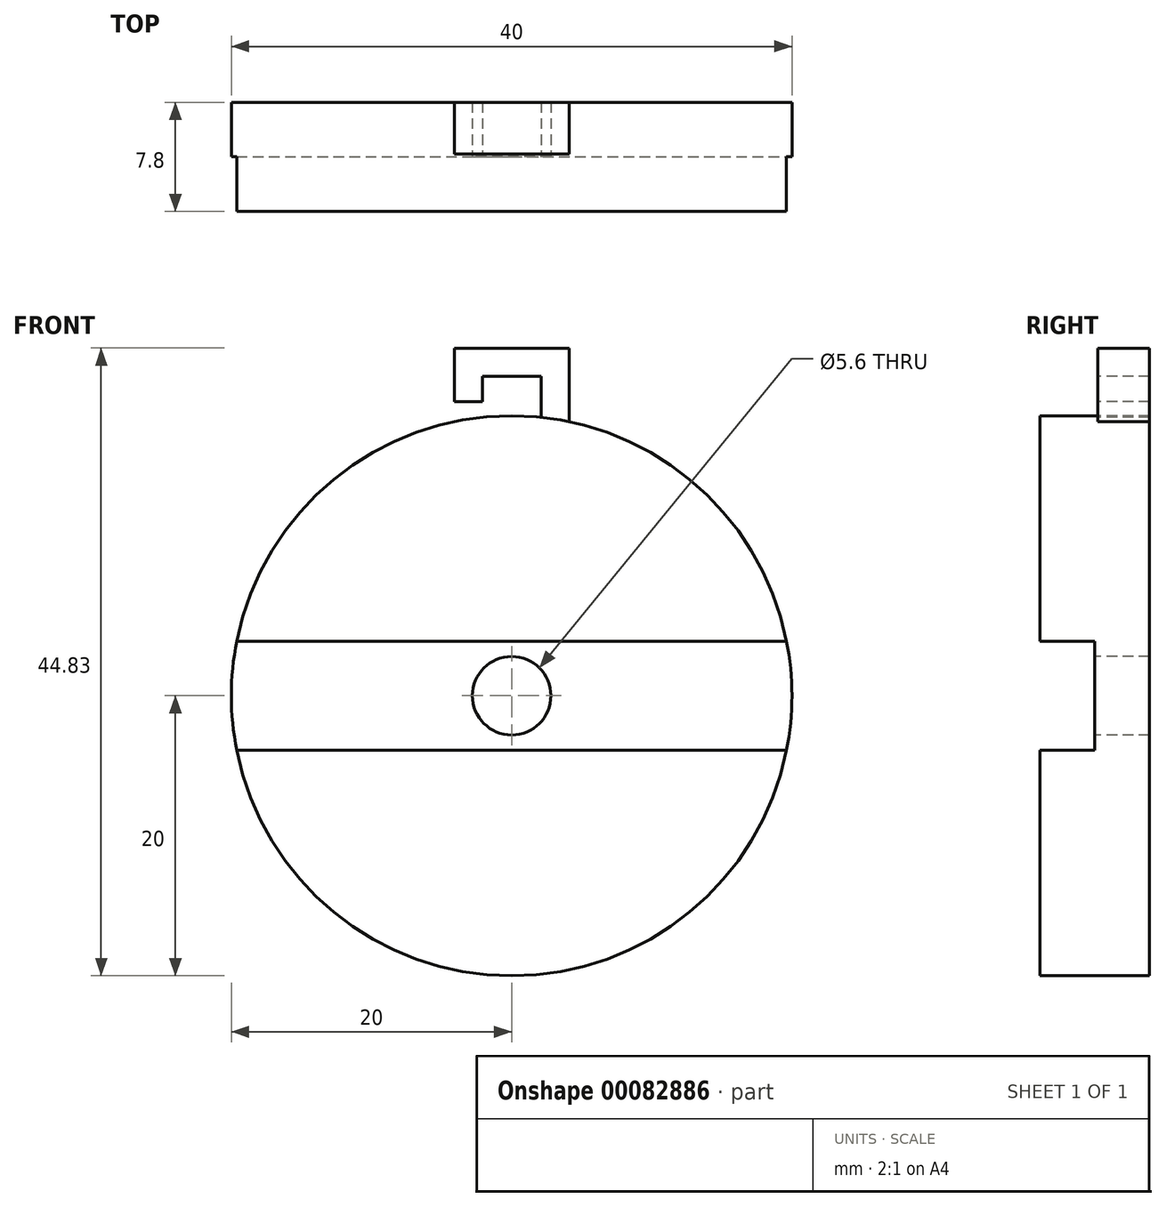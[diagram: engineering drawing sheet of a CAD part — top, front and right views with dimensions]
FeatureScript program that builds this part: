
annotation { "Feature Type Name" : "Feature", "Feature Type Description" : "" }
export const myFeature = defineFeature(function(context is Context, id is Id, definition is map)
    precondition{}
    {
        {
            var Q0;
            Q0=qCreatedBy(makeId("Front.planeOp"),FACE);
            var sketch = newSketch(context, id + "F0", { "sketchPlane" : qUnion([Q0])});
            skCircle(sketch, "E0", {"center": v(0, 0) * mm, "radius": 20 * mm});
            skSolve(sketch);
        }
        {
            var Q0;
            Q0=qSketchRegion(id+"F0",true);
            var Q1;
            Q1=makeQuery(id+"F0.imprint","IMPRINT",FACE,{"disambiguationData":[TD([[makeQuery(id+"F0.imprint","IMPRINT",EDGE,{"derivedFrom":sQuery(id+"F0.wireOp",EDGE,"E0")}),1.0]])]});
            extrude(context, id + "F1", {"entities" : qUnion([Q0, Q1]), "oppositeDirection" : true, "depth" : 7.8 * mm});
        }
        {
            var Q0;
            Q0=makeQuery(id+"F1.opExtrude","CAP_FACE",FACE,{"disambiguationData":[OSD([sQuery(id+"F0.wireOp",EDGE,"E0")])],"isStart":true});
            var sketch = newSketch(context, id + "F2", { "sketchPlane" : qUnion([Q0])});
            skLineSegment(sketch, "E1.bottom", {"start": v(-20, 3.9) * mm, "end": v(20, 3.9) * mm});
            skLineSegment(sketch, "E1.top", {"start": v(-20, -3.9) * mm, "end": v(20, -3.9) * mm});
            skLineSegment(sketch, "E1.left", {"start": v(-20, 3.9) * mm, "end": v(-20, -3.9) * mm});
            skLineSegment(sketch, "E1.right", {"start": v(20, 3.9) * mm, "end": v(20, -3.9) * mm});
            skSolve(sketch);
        }
        {
            var Q0;
            {var subQ0=sQuery(id+"F2.wireOp",EDGE,"E1.bottom");var subQ1=makeQuery(id+"F1.opExtrude","CAP_EDGE",EDGE,{"disambiguationData":[OSD([sQuery(id+"F0.wireOp",EDGE,"E0")])],"isStart":true});var subQ4=makeQuery(id+"F2.imprint","INTERSECT",VERTEX,{"disambiguationData":[OD(0.0)],"derivedFrom":[subQ1,subQ0]});Q0=makeQuery(id+"F2.imprint","IMPRINT",FACE,{"disambiguationData":[TD([[makeQuery(id+"F2.imprint","IMPRINT",EDGE,{"disambiguationData":[TD([[subQ4,-1.0]])],"derivedFrom":subQ0}),-1.0]])]});}
            extrude(context, id + "F3", {"entities" : qUnion([Q0]), "operationType" : NewBodyOperationType.REMOVE, "oppositeDirection" : true, "depth" : 3.9 * mm});
        }
        {
            var Q0;
            Q0=makeQuery(id+"F3.boolean.opBoolean","COPY",FACE,{"derivedFrom":makeQuery(id+"F3.opExtrude","CAP_FACE",FACE,{"disambiguationData":[OSD([sQuery(id+"F0.wireOp",EDGE,"E0"),sQuery(id+"F2.wireOp",EDGE,"E1.bottom"),sQuery(id+"F2.wireOp",EDGE,"E1.top")])],"isStart":false})});
            var sketch = newSketch(context, id + "F4", { "sketchPlane" : qUnion([Q0])});
            skCircle(sketch, "E2", {"center": v(0, 0) * mm, "radius": 2.8 * mm});
            skSolve(sketch);
        }
        {
            var Q0;
            Q0=qSketchRegion(id+"F4",true);
            extrude(context, id + "F5", {"entities" : qUnion([Q0]), "operationType" : NewBodyOperationType.REMOVE, "endBound" : BoundingType.THROUGH_ALL, "oppositeDirection" : true, "depth" : 25 * mm});
        }
        {
            var Q0;
            Q0=makeQuery(id+"F1.opExtrude","CAP_FACE",FACE,{"disambiguationData":[OSD([sQuery(id+"F0.wireOp",EDGE,"E0")])],"isStart":false});
            var sketch = newSketch(context, id + "F6", { "sketchPlane" : qUnion([Q0])});
            skLineSegment(sketch, "E3.bottom", {"start": v(-4.1, 24.83) * mm, "end": v(4.1, 24.83) * mm});
            skLineSegment(sketch, "E3.top", {"start": v(-4.1, 19.58) * mm, "end": v(4.1, 19.58) * mm});
            skLineSegment(sketch, "E3.left", {"start": v(-4.1, 24.83) * mm, "end": v(-4.1, 19.58) * mm});
            skLineSegment(sketch, "E3.right", {"start": v(4.1, 24.83) * mm, "end": v(4.1, 19.58) * mm});
            skSolve(sketch);
        }
        {
            var Q0;
            Q0=qSketchRegion(id+"F6",true);
            extrude(context, id + "F7", {"entities" : qUnion([Q0]), "operationType" : NewBodyOperationType.ADD, "oppositeDirection" : true, "depth" : 3.7 * mm});
        }
        {
            var Q0;
            Q0=makeQuery(id+"F7.opExtrude","CAP_FACE",FACE,{"disambiguationData":[OSD([sQuery(id+"F6.wireOp",EDGE,"E3.bottom"),sQuery(id+"F6.wireOp",EDGE,"E3.top"),sQuery(id+"F6.wireOp",EDGE,"E3.left"),sQuery(id+"F6.wireOp",EDGE,"E3.right")])],"isStart":false});
            var sketch = newSketch(context, id + "F8", { "sketchPlane" : qUnion([Q0])});
            skLineSegment(sketch, "E4", {"start": v(-2.1, 22.2) * mm, "end": v(-2.1, 22.83) * mm});
            skLineSegment(sketch, "E5", {"start": v(-2.1, 22.83) * mm, "end": v(2.1, 22.83) * mm});
            skLineSegment(sketch, "E6", {"start": v(2.1, 22.83) * mm, "end": v(2.1, 19.89) * mm});
            skLineSegment(sketch, "E7.top", {"start": v(-4.1, 21) * mm, "end": v(-2.1, 21) * mm});
            skLineSegment(sketch, "E7.right", {"start": v(-2.1, 22.2) * mm, "end": v(-2.1, 21) * mm});
            skPoint(sketch, "E7.left.start.orphan", {"position": v(-4.1, 22.2) * mm});
            skLineSegment(sketch, "E8", {"start": v(-4.1, 21) * mm, "end": v(-4.1, 19.58) * mm});
            skArc(sketch, "E9", {"start": v(2.1, 19.89) * mm, "mid": v(-1.01, 19.97) * mm, "end": v(-4.1, 19.58) * mm});
            skSolve(sketch);
        }
        {
            var Q0;
            Q0=qSketchRegion(id+"F8",true);
            extrude(context, id + "F9", {"entities" : qUnion([Q0]), "operationType" : NewBodyOperationType.REMOVE, "endBound" : BoundingType.THROUGH_ALL, "oppositeDirection" : true, "depth" : 25 * mm});
        }
    });
